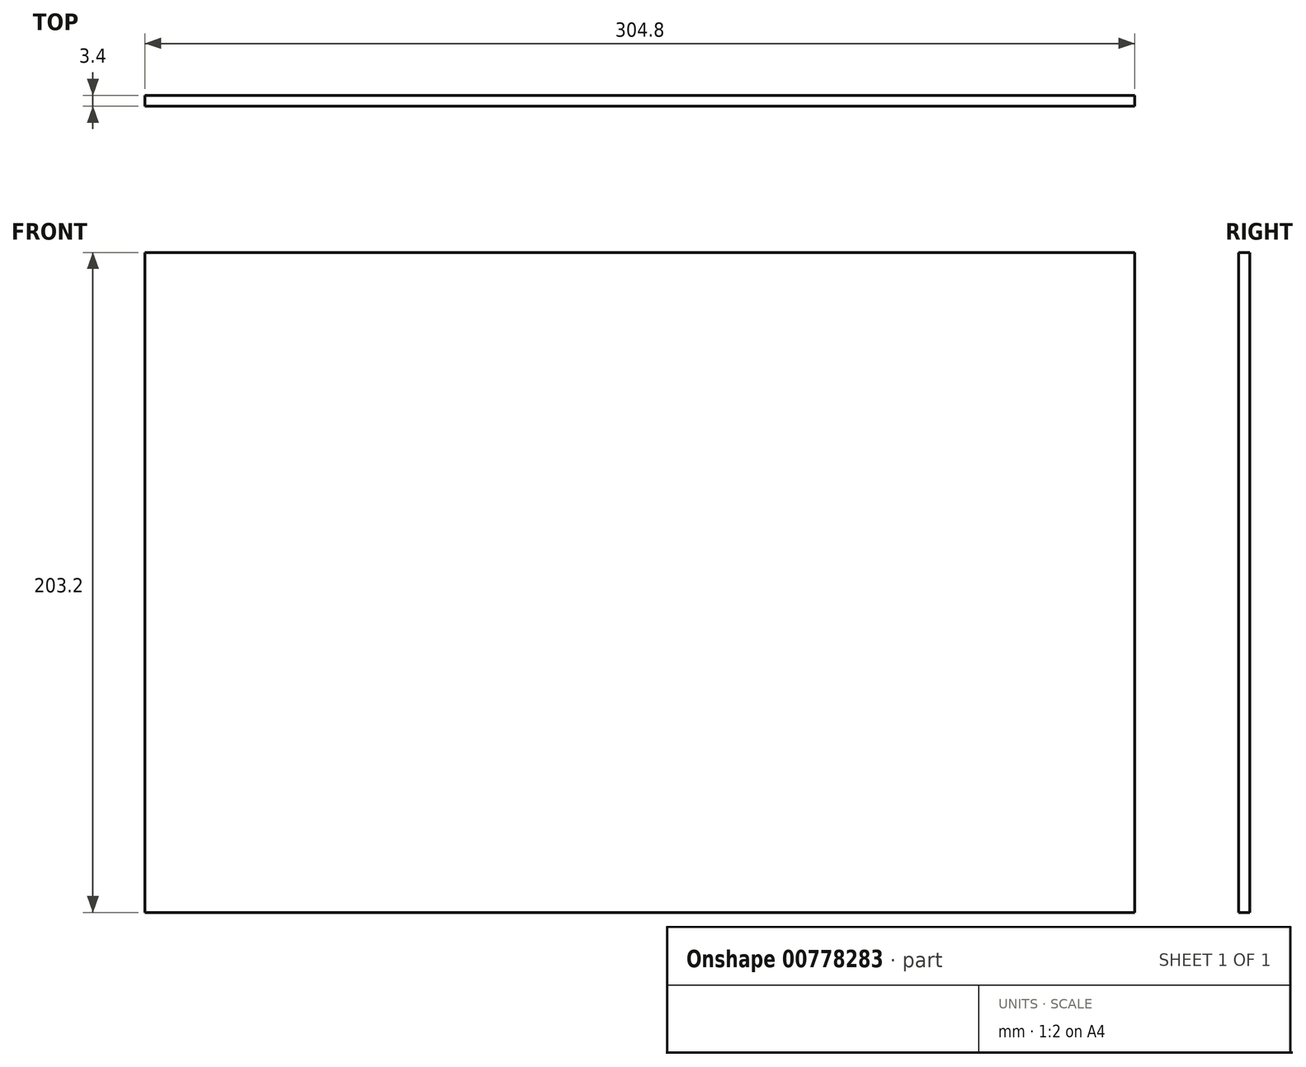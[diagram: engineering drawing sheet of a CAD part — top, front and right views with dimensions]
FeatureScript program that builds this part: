
annotation { "Feature Type Name" : "Feature", "Feature Type Description" : "" }
export const myFeature = defineFeature(function(context is Context, id is Id, definition is map)
    precondition{}
    {
        {
            var Q0;
            Q0=qCreatedBy(makeId("Front.planeOp"),FACE);
            var sketch = newSketch(context, id + "F0", { "sketchPlane" : qUnion([Q0])});
            skLineSegment(sketch, "E0.bottom", {"start": v(-152.4, 101.6) * mm, "end": v(152.4, 101.6) * mm});
            skLineSegment(sketch, "E0.top", {"start": v(-152.4, -101.6) * mm, "end": v(152.4, -101.6) * mm});
            skLineSegment(sketch, "E0.left", {"start": v(-152.4, 101.6) * mm, "end": v(-152.4, -101.6) * mm});
            skLineSegment(sketch, "E0.right", {"start": v(152.4, 101.6) * mm, "end": v(152.4, -101.6) * mm});
            skPoint(sketch, "E0.middle", {"position": v(0, 0) * mm});
            skPoint(sketch, "E1", {"position": v(127, 76.2) * mm});
            skSolve(sketch);
        }
        {
            var Q0;
            Q0=makeQuery(id+"F0.imprint","IMPRINT",FACE,{"disambiguationData":[TD([[makeQuery(id+"F0.imprint","IMPRINT",EDGE,{"derivedFrom":sQuery(id+"F0.wireOp",EDGE,"E0.bottom")}),-1.0]])]});
            extrude(context, id + "F1", {"entities" : qUnion([Q0]), "depth" : 3.4 * mm, "offsetDistance" : 25.4 * mm});
        }
    });
